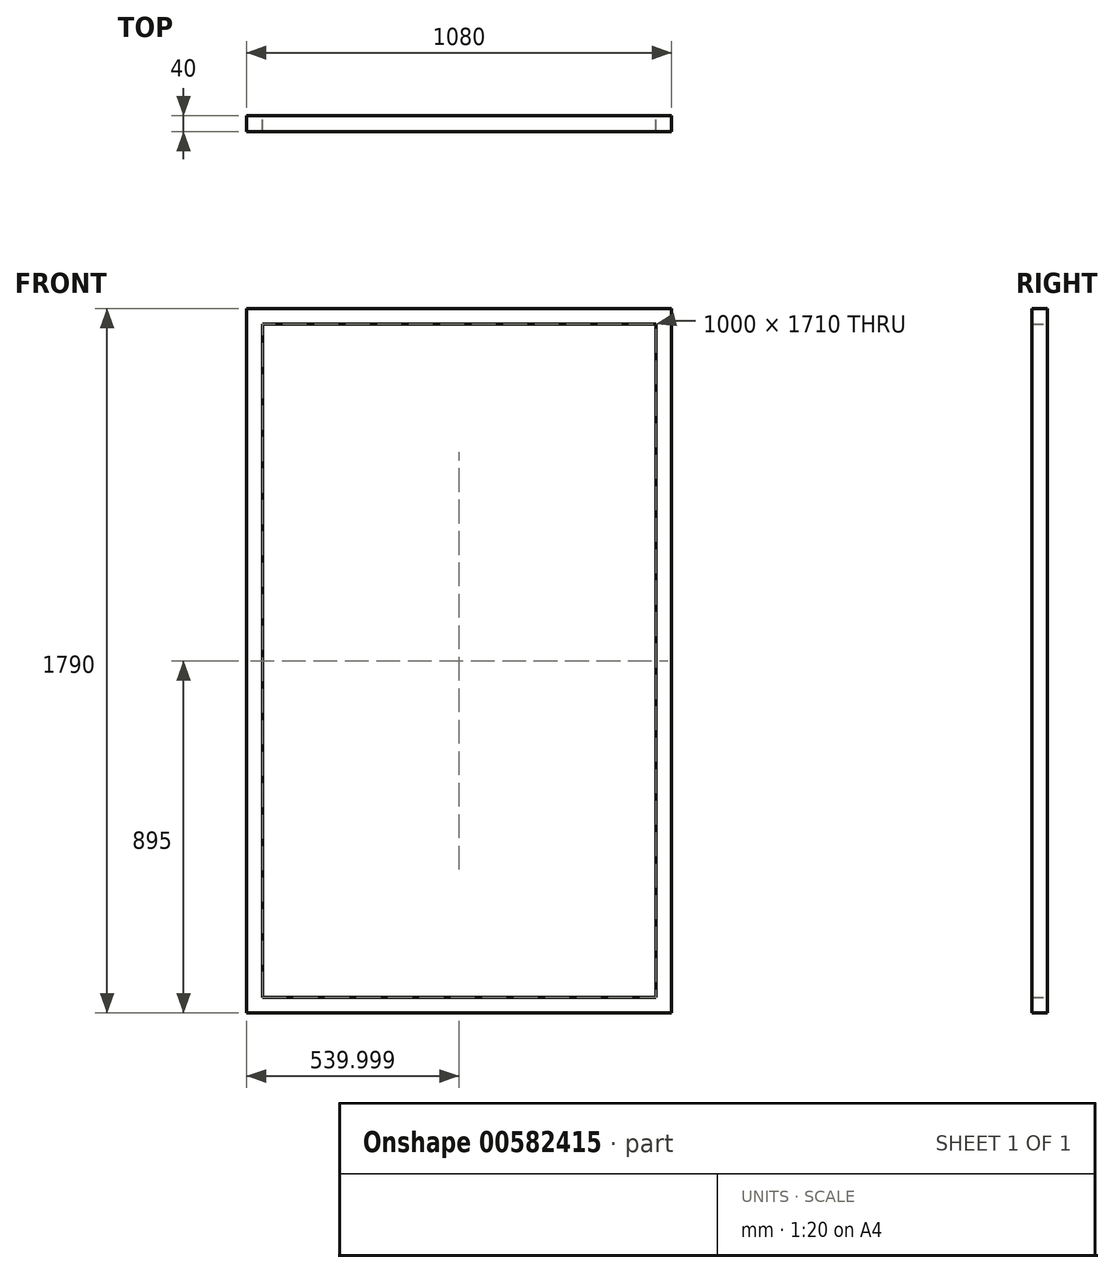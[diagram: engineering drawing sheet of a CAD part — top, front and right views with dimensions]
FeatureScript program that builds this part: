
annotation { "Feature Type Name" : "Feature", "Feature Type Description" : "" }
export const myFeature = defineFeature(function(context is Context, id is Id, definition is map)
    precondition{}
    {
        {
            var Q0;
            Q0=qCreatedBy(makeId("Front.planeOp"),FACE);
            var sketch = newSketch(context, id + "F0", { "sketchPlane" : qUnion([Q0])});
            skLineSegment(sketch, "E0.bottom", {"start": v(-80.22, 0) * mm, "end": v(999.78, 0) * mm});
            skLineSegment(sketch, "E0.top", {"start": v(-80.22, -1790) * mm, "end": v(999.78, -1790) * mm});
            skLineSegment(sketch, "E0.left", {"start": v(-80.22, 0) * mm, "end": v(-80.22, -1790) * mm});
            skLineSegment(sketch, "E0.right", {"start": v(999.78, 0) * mm, "end": v(999.78, -1790) * mm});
            skLineSegment(sketch, "E1.0", {"start": v(-80.22, -40) * mm, "end": v(999.78, -40) * mm});
            skLineSegment(sketch, "E2.0", {"start": v(959.78, -40) * mm, "end": v(959.78, -1750) * mm});
            skLineSegment(sketch, "E3.0", {"start": v(-40.22, -40) * mm, "end": v(-40.22, -1750) * mm});
            skLineSegment(sketch, "E4.0", {"start": v(-80.22, -1750) * mm, "end": v(999.78, -1750) * mm});
            skLineSegment(sketch, "E5.0", {"start": v(-38.22, -42) * mm, "end": v(957.78, -42) * mm});
            skLineSegment(sketch, "E6.0", {"start": v(-38.22, -42) * mm, "end": v(-38.22, -1748) * mm});
            skLineSegment(sketch, "E7.0", {"start": v(-38.22, -1748) * mm, "end": v(957.78, -1748) * mm});
            skLineSegment(sketch, "E8.0", {"start": v(957.78, -42) * mm, "end": v(957.78, -1748) * mm});
            skSolve(sketch);
        }
        {
            var Q0;
            Q0=qSketchRegion(id+"F0",true);
            extrude(context, id + "F1", {"entities" : qUnion([Q0]), "depth" : 40 * mm, "offsetDistance" : 25 * mm});
        }
    });
